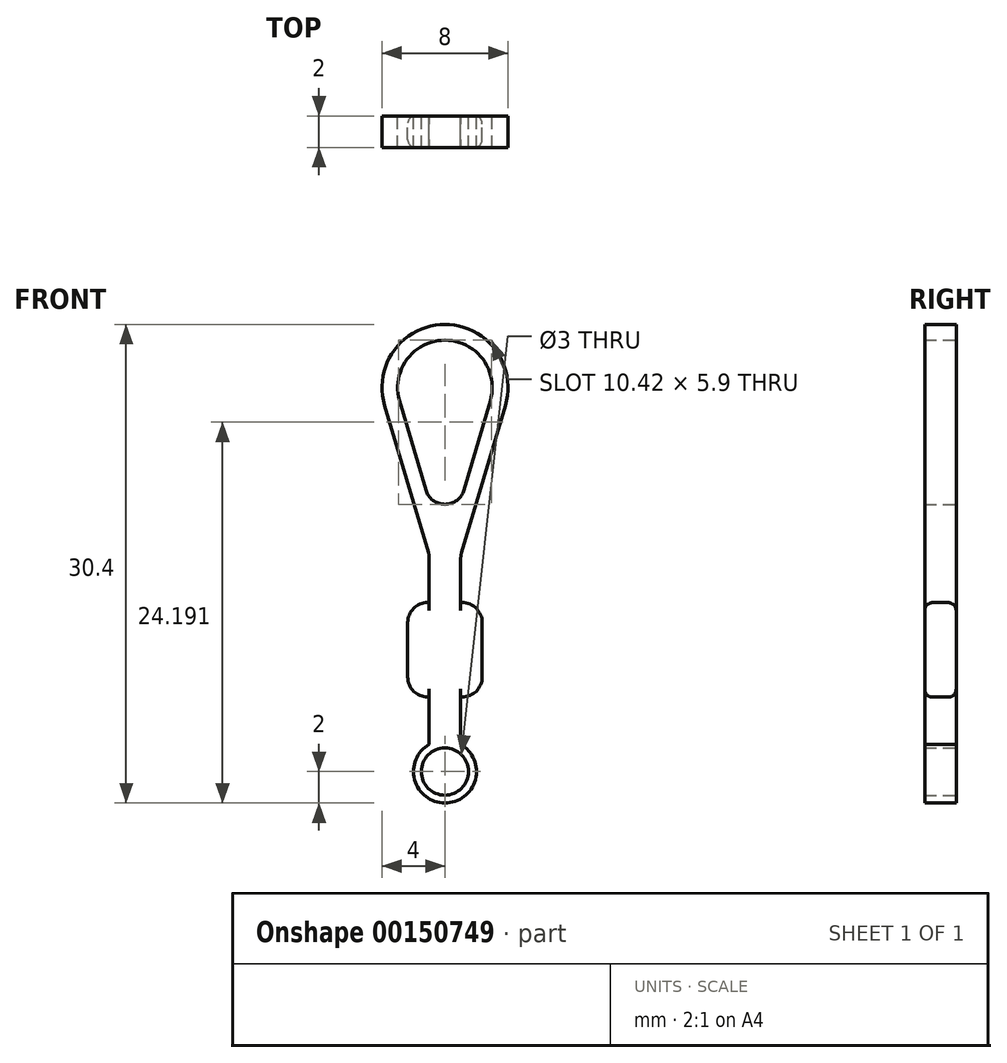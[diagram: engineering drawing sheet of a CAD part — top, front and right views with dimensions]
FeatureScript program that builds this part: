
annotation { "Feature Type Name" : "Feature", "Feature Type Description" : "" }
export const myFeature = defineFeature(function(context is Context, id is Id, definition is map)
    precondition{}
    {
        {
            var Q0;
            Q0=qCreatedBy(makeId("Front.planeOp"),FACE);
            var sketch = newSketch(context, id + "F0", { "sketchPlane" : qUnion([Q0])});
            skCircle(sketch, "E0", {"center": v(0, 0) * mm, "radius": 1.5 * mm});
            skArc(sketch, "E1", {"start": v(-1, 1.73) * mm, "mid": v(0, -2) * mm, "end": v(1, 1.73) * mm});
            skLineSegment(sketch, "E2", {"start": v(1, 1.73) * mm, "end": v(1, 4.73) * mm});
            skLineSegment(sketch, "E3", {"start": v(-1, 1.73) * mm, "end": v(-1, 4.73) * mm});
            skLineSegment(sketch, "E4", {"start": v(1, 4.73) * mm, "end": v(2.36, 4.73) * mm});
            skLineSegment(sketch, "E5", {"start": v(2.36, 4.73) * mm, "end": v(2.36, 10.73) * mm});
            skLineSegment(sketch, "E6", {"start": v(-1, 4.73) * mm, "end": v(-2.36, 4.73) * mm});
            skLineSegment(sketch, "E7", {"start": v(-2.36, 4.73) * mm, "end": v(-2.36, 10.73) * mm});
            skLineSegment(sketch, "E8", {"start": v(-2.36, 10.73) * mm, "end": v(-1, 10.73) * mm});
            skLineSegment(sketch, "E9", {"start": v(-1, 10.73) * mm, "end": v(-1, 13.73) * mm});
            skLineSegment(sketch, "E10", {"start": v(1, 10.73) * mm, "end": v(1, 13.73) * mm});
            skLineSegment(sketch, "E11.trimOffspring", {"start": v(1, 10.73) * mm, "end": v(2.36, 10.73) * mm});
            skArc(sketch, "E12", {"start": v(3.83, 23.26) * mm, "mid": v(0, 28.4) * mm, "end": v(-3.83, 23.26) * mm});
            skArc(sketch, "E13", {"start": v(2.88, 23.56) * mm, "mid": v(0, 27.4) * mm, "end": v(-2.88, 23.56) * mm});
            skLineSegment(sketch, "E14", {"start": v(-1, 13.73) * mm, "end": v(-3.83, 23.26) * mm});
            skLineSegment(sketch, "E15", {"start": v(1, 13.73) * mm, "end": v(3.83, 23.26) * mm});
            skLineSegment(sketch, "E16", {"start": v(0, 13.73) * mm, "end": v(-2.88, 23.56) * mm});
            skLineSegment(sketch, "E17", {"start": v(0, 13.73) * mm, "end": v(2.88, 23.56) * mm});
            skSolve(sketch);
        }
        {
            var Q0;
            Q0=makeQuery(id+"F0.imprint","IMPRINT",FACE,{"disambiguationData":[TD([[makeQuery(id+"F0.imprint","IMPRINT",EDGE,{"derivedFrom":sQuery(id+"F0.wireOp",EDGE,"E0")}),-1.0]])]});
            extrude(context, id + "F1", {"entities" : qUnion([Q0]), "depth" : 2 * mm});
        }
        {
            var Q0;
            Q0=makeQuery(id+"F1.opExtrude","SWEPT_EDGE",EDGE,{"disambiguationData":[OSD([sQuery(id+"F0.wireOp",EDGE,"E5"),sQuery(id+"F0.wireOp",EDGE,"E11.trimOffspring")])]});
            var Q1;
            Q1=makeQuery(id+"F1.opExtrude","SWEPT_EDGE",EDGE,{"disambiguationData":[OSD([sQuery(id+"F0.wireOp",EDGE,"E4"),sQuery(id+"F0.wireOp",EDGE,"E5")])]});
            var Q2;
            Q2=makeQuery(id+"F1.opExtrude","SWEPT_EDGE",EDGE,{"disambiguationData":[OSD([sQuery(id+"F0.wireOp",EDGE,"E7"),sQuery(id+"F0.wireOp",EDGE,"E8")])]});
            var Q3;
            Q3=makeQuery(id+"F1.opExtrude","SWEPT_EDGE",EDGE,{"disambiguationData":[OSD([sQuery(id+"F0.wireOp",EDGE,"E6"),sQuery(id+"F0.wireOp",EDGE,"E7")])]});
            var Q4;
            Q4=makeQuery(id+"F1.opExtrude","SWEPT_EDGE",EDGE,{"disambiguationData":[OSD([sQuery(id+"F0.wireOp",EDGE,"E16"),sQuery(id+"F0.wireOp",EDGE,"E17")])]});
            var Q5;
            Q5=makeQuery(id+"F1.opExtrude","SWEPT_EDGE",EDGE,{"disambiguationData":[OSD([sQuery(id+"F0.wireOp",EDGE,"E10"),sQuery(id+"F0.wireOp",EDGE,"E15")])]});
            var Q6;
            Q6=makeQuery(id+"F1.opExtrude","SWEPT_EDGE",EDGE,{"disambiguationData":[OSD([sQuery(id+"F0.wireOp",EDGE,"E9"),sQuery(id+"F0.wireOp",EDGE,"E14")])]});
            fillet(context, id + "F2", {"entities" : qUnion([Q0, Q1, Q2, Q3, Q4, Q5, Q6]), "radius" : 1.27 * mm, "tangentPropagation" : true, "allowEdgeOverflow" : false});
        }
        {
            var Q0;
            {var subQ0=sQuery(id+"F0.wireOp",EDGE,"E8");var subQ1=sQuery(id+"F0.wireOp",EDGE,"E7");Q0=makeQuery(id+"F2.opFillet","BLEND_EDGE",EDGE,{"blendedFrom":[makeQuery(id+"F1.opExtrude","SWEPT_EDGE",EDGE,{"disambiguationData":[OSD([subQ1,subQ0])]}),makeQuery(id+"F1.opExtrude","CAP_FACE",FACE,{"disambiguationData":[OSD([sQuery(id+"F0.wireOp",EDGE,"E0"),sQuery(id+"F0.wireOp",EDGE,"E1"),sQuery(id+"F0.wireOp",EDGE,"E2"),sQuery(id+"F0.wireOp",EDGE,"E3"),sQuery(id+"F0.wireOp",EDGE,"E4"),sQuery(id+"F0.wireOp",EDGE,"E5"),sQuery(id+"F0.wireOp",EDGE,"E6"),subQ1,subQ0,sQuery(id+"F0.wireOp",EDGE,"E9"),sQuery(id+"F0.wireOp",EDGE,"E10"),sQuery(id+"F0.wireOp",EDGE,"E11.trimOffspring"),sQuery(id+"F0.wireOp",EDGE,"E12"),sQuery(id+"F0.wireOp",EDGE,"E13"),sQuery(id+"F0.wireOp",EDGE,"E14"),sQuery(id+"F0.wireOp",EDGE,"E15"),sQuery(id+"F0.wireOp",EDGE,"E16"),sQuery(id+"F0.wireOp",EDGE,"E17")])],"isStart":false})],"blendedInto":[makeQuery(id+"F1.opExtrude","CAP_FACE",FACE,{"disambiguationData":[OSD([sQuery(id+"F0.wireOp",EDGE,"E0"),sQuery(id+"F0.wireOp",EDGE,"E1"),sQuery(id+"F0.wireOp",EDGE,"E2"),sQuery(id+"F0.wireOp",EDGE,"E3"),sQuery(id+"F0.wireOp",EDGE,"E4"),sQuery(id+"F0.wireOp",EDGE,"E5"),sQuery(id+"F0.wireOp",EDGE,"E6"),subQ1,subQ0,sQuery(id+"F0.wireOp",EDGE,"E9"),sQuery(id+"F0.wireOp",EDGE,"E10"),sQuery(id+"F0.wireOp",EDGE,"E11.trimOffspring"),sQuery(id+"F0.wireOp",EDGE,"E12"),sQuery(id+"F0.wireOp",EDGE,"E13"),sQuery(id+"F0.wireOp",EDGE,"E14"),sQuery(id+"F0.wireOp",EDGE,"E15"),sQuery(id+"F0.wireOp",EDGE,"E16"),sQuery(id+"F0.wireOp",EDGE,"E17")])],"isStart":false})]});}
            var Q1;
            {var subQ0=sQuery(id+"F0.wireOp",EDGE,"E11.trimOffspring");var subQ1=sQuery(id+"F0.wireOp",EDGE,"E5");Q1=makeQuery(id+"F2.opFillet","BLEND_EDGE",EDGE,{"blendedFrom":[makeQuery(id+"F1.opExtrude","SWEPT_EDGE",EDGE,{"disambiguationData":[OSD([subQ1,subQ0])]}),makeQuery(id+"F1.opExtrude","CAP_FACE",FACE,{"disambiguationData":[OSD([sQuery(id+"F0.wireOp",EDGE,"E0"),sQuery(id+"F0.wireOp",EDGE,"E1"),sQuery(id+"F0.wireOp",EDGE,"E2"),sQuery(id+"F0.wireOp",EDGE,"E3"),sQuery(id+"F0.wireOp",EDGE,"E4"),subQ1,sQuery(id+"F0.wireOp",EDGE,"E6"),sQuery(id+"F0.wireOp",EDGE,"E7"),sQuery(id+"F0.wireOp",EDGE,"E8"),sQuery(id+"F0.wireOp",EDGE,"E9"),sQuery(id+"F0.wireOp",EDGE,"E10"),subQ0,sQuery(id+"F0.wireOp",EDGE,"E12"),sQuery(id+"F0.wireOp",EDGE,"E13"),sQuery(id+"F0.wireOp",EDGE,"E14"),sQuery(id+"F0.wireOp",EDGE,"E15"),sQuery(id+"F0.wireOp",EDGE,"E16"),sQuery(id+"F0.wireOp",EDGE,"E17")])],"isStart":false})],"blendedInto":[makeQuery(id+"F1.opExtrude","CAP_FACE",FACE,{"disambiguationData":[OSD([sQuery(id+"F0.wireOp",EDGE,"E0"),sQuery(id+"F0.wireOp",EDGE,"E1"),sQuery(id+"F0.wireOp",EDGE,"E2"),sQuery(id+"F0.wireOp",EDGE,"E3"),sQuery(id+"F0.wireOp",EDGE,"E4"),subQ1,sQuery(id+"F0.wireOp",EDGE,"E6"),sQuery(id+"F0.wireOp",EDGE,"E7"),sQuery(id+"F0.wireOp",EDGE,"E8"),sQuery(id+"F0.wireOp",EDGE,"E9"),sQuery(id+"F0.wireOp",EDGE,"E10"),subQ0,sQuery(id+"F0.wireOp",EDGE,"E12"),sQuery(id+"F0.wireOp",EDGE,"E13"),sQuery(id+"F0.wireOp",EDGE,"E14"),sQuery(id+"F0.wireOp",EDGE,"E15"),sQuery(id+"F0.wireOp",EDGE,"E16"),sQuery(id+"F0.wireOp",EDGE,"E17")])],"isStart":false})]});}
            var Q2;
            Q2=makeQuery(id+"F1.opExtrude","CAP_EDGE",EDGE,{"disambiguationData":[OSD([sQuery(id+"F0.wireOp",EDGE,"E5")])],"isStart":true});
            var Q3;
            Q3=makeQuery(id+"F1.opExtrude","CAP_EDGE",EDGE,{"disambiguationData":[OSD([sQuery(id+"F0.wireOp",EDGE,"E7")])],"isStart":true});
            fillet(context, id + "F3", {"entities" : qUnion([Q0, Q1, Q2, Q3]), "radius" : 0.5 * mm, "tangentPropagation" : true, "allowEdgeOverflow" : false});
        }
    });
